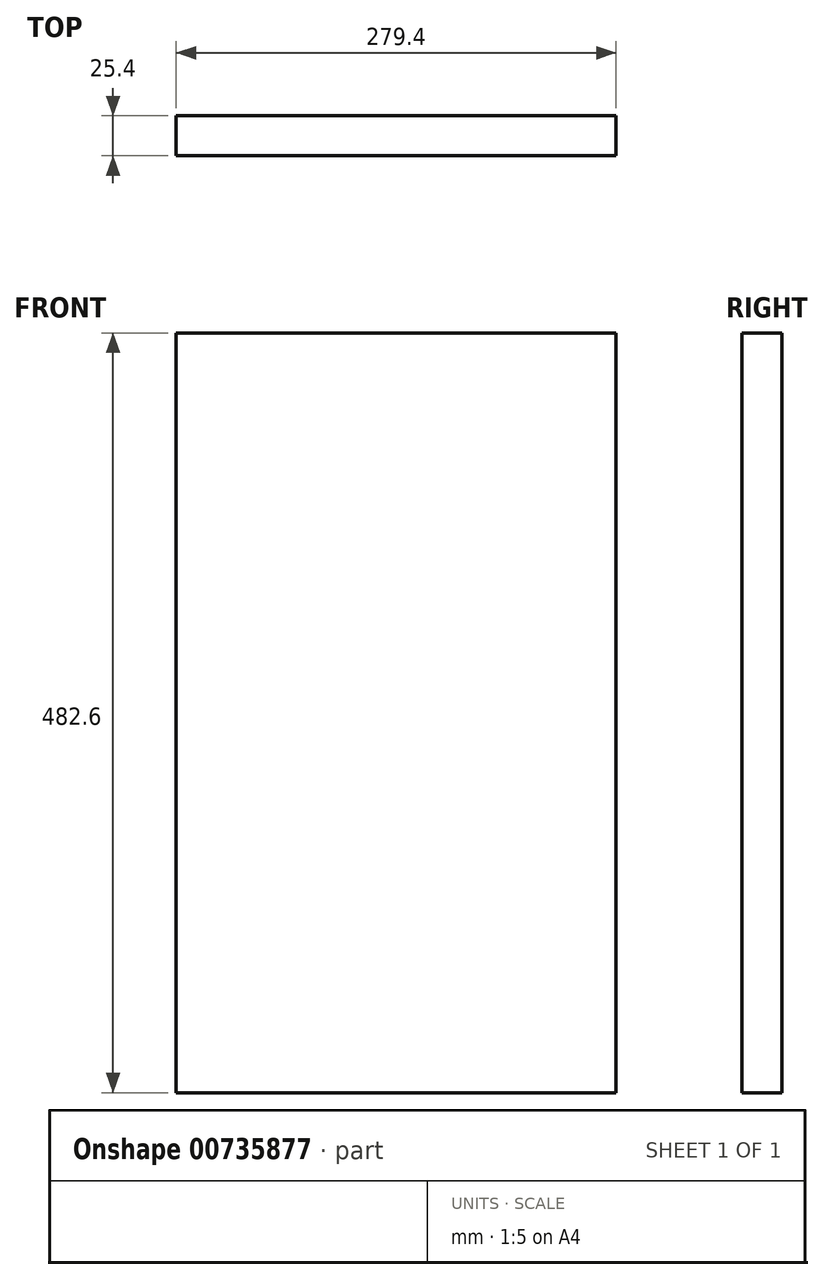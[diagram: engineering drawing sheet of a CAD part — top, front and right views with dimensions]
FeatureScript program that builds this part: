
annotation { "Feature Type Name" : "Feature", "Feature Type Description" : "" }
export const myFeature = defineFeature(function(context is Context, id is Id, definition is map)
    precondition{}
    {
        {
            var Q0;
            Q0=qCreatedBy(makeId("Front.planeOp"),FACE);
            var sketch = newSketch(context, id + "F0", { "sketchPlane" : qUnion([Q0])});
            skLineSegment(sketch, "E0.bottom", {"start": v(-246.48, 240.39) * mm, "end": v(32.92, 240.39) * mm});
            skLineSegment(sketch, "E0.top", {"start": v(-246.48, -242.21) * mm, "end": v(32.92, -242.21) * mm});
            skLineSegment(sketch, "E0.left", {"start": v(-246.48, 240.39) * mm, "end": v(-246.48, -242.21) * mm});
            skLineSegment(sketch, "E0.right", {"start": v(32.92, 240.39) * mm, "end": v(32.92, -242.21) * mm});
            skSolve(sketch);
        }
        {
            var Q0;
            Q0=makeQuery(id+"F0.imprint","IMPRINT",FACE,{"disambiguationData":[TD([[makeQuery(id+"F0.imprint","IMPRINT",EDGE,{"derivedFrom":sQuery(id+"F0.wireOp",EDGE,"E0.bottom")}),-1.0]])]});
            extrude(context, id + "F1", {"entities" : qUnion([Q0]), "depth" : 25.4 * mm, "offsetDistance" : 25.4 * mm});
        }
    });
